# Revit family: Domotics-CablaggioStrutturato-GEWISS-QUADRI_PARETE_19_6U_P400
name_source: partatom
category: Apparecchi elettrici
units: mm (PartAtom-declared; Revit-internal decimal feet)

## family parameters
Condiviso = No
Host = Superficie
Mantenere orientamento annotazione = Sì
Punto di calcolo locali = Sì
Quota connettore circolare = Usa diametro
Taglio con vuoti quando caricato = No
Tipo di parte = Normale

## types (1)
- Domotics-CablaggioStrutturato-GEWISS-QUADRI_PARETE_19_6U_P400
    Apertura porta = 180°
    Catalogo = DOMOTICS
    Categoria = Quadro da parete 19"
    Codice Electrocod = 3752
    Colore = Grigio (RAL 7035)
    Descrizione = QUADRO DA PARETE 19 6U P= 400MM.
    Dim. esterne BxHxP (mm) = 600x335x400
    Finitura = Bucciata
    Grado di protezione = IP20
    IDF = 1b698a6c-7a05-496e-9209-83a3675877ec
    IDT = 1607453e44e34c9e8499f282ce5acb34
    Immagine tipo = B.jpg
    L_quadro = 325 mm
    Materiale = Acciaio
    Modello = GW38406
    N. montanti = 2
    Portata statica = 50KG
    Produttore = GEWISS S.p.A.
    Profondità (mm) = 400 mm
    Prospetto di default = 1219 mm
    SEO = Quadro
    Scheda Tecnica = https://www.gewiss.com
    Tipologia porta = Reversibile
    URL = https://www.gewiss.com
    Unità di cablaggio = 6 U
    Versione file RFA = 21.2
    a = 15.00°
    h_quadro = 400 mm  [stored 1.31234 ft]
    p_quadro = 263 mm

note: [stored X ft] marks values corroborated as IEEE doubles in the binary element streams (Revit-internal decimal feet)

## geometry (parser evidence)
native form markers: Sweep x4
no freeform markers — native parametric forms only
